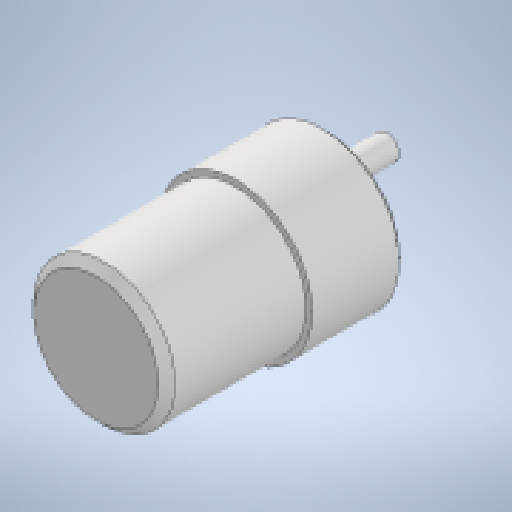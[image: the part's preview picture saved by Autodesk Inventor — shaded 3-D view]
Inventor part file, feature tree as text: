
AUTODESK INVENTOR PART (.ipt)
format: ipt  version: 2025.1 (Build 291241000, 241)  size: 282,624 bytes
history: native  units: mm
features: sketch x7, extrude x6, chamfer x3
ambient origin geometry x8: Origin, YZ Plane, XZ Plane, XY Plane, X Axis, Y Axis, Z Axis, Center Point
bodies: 实体1 (feature_tree)
feature tree (16):
  extrude  "拉伸1"  Depth=22.0mm TaperAngle=0.0deg
  extrude  "拉伸2"  Depth=33.5mm TaperAngle=0.0deg
  chamfer  "倒角1"  Distance=2.0mm Angle=45.0deg
  extrude  "拉伸3"  Depth=7.0mm
  extrude  "拉伸4"  Depth=15.5mm
  chamfer  "倒角2"  Distance=15.5mm
  extrude  "拉伸5"  Depth=1.0mm
  chamfer  "倒角3"  Distance=1.0mm
  extrude  "拉伸6"  Depth=1.0mm
  sketch  "草图1"  dims[d0=37.0mm d1=22.0mm d2=0.0mm]
  sketch  "草图2"  dims[d9=10.0mm d10=7.0mm]
  sketch  "草图3"  dims[d11=6.0mm d12=0.0mm d13=6.0mm d14=15.5mm d15=0.0mm]
  sketch  "草图4"  dims[d16=0.5mm d17=2.0mm d18=45.0deg d19=22.0mm d20=1.0mm d21=0.0mm]
  sketch  "草图5"  dims[d22=1.0mm d23=2.0mm d24=45.0deg d25=31.0mm]
  sketch  "草图6"  dims[d26=3.2mm d27=60.0mm d29=360.0deg d31=10.0mm d32=0.0mm]
  sketch  "草图 - 环形阵列1"  dims[d3=34.0mm d4=33.5mm d5=0.0mm d6=2.0mm d7=2.0mm d8=45.0deg]
